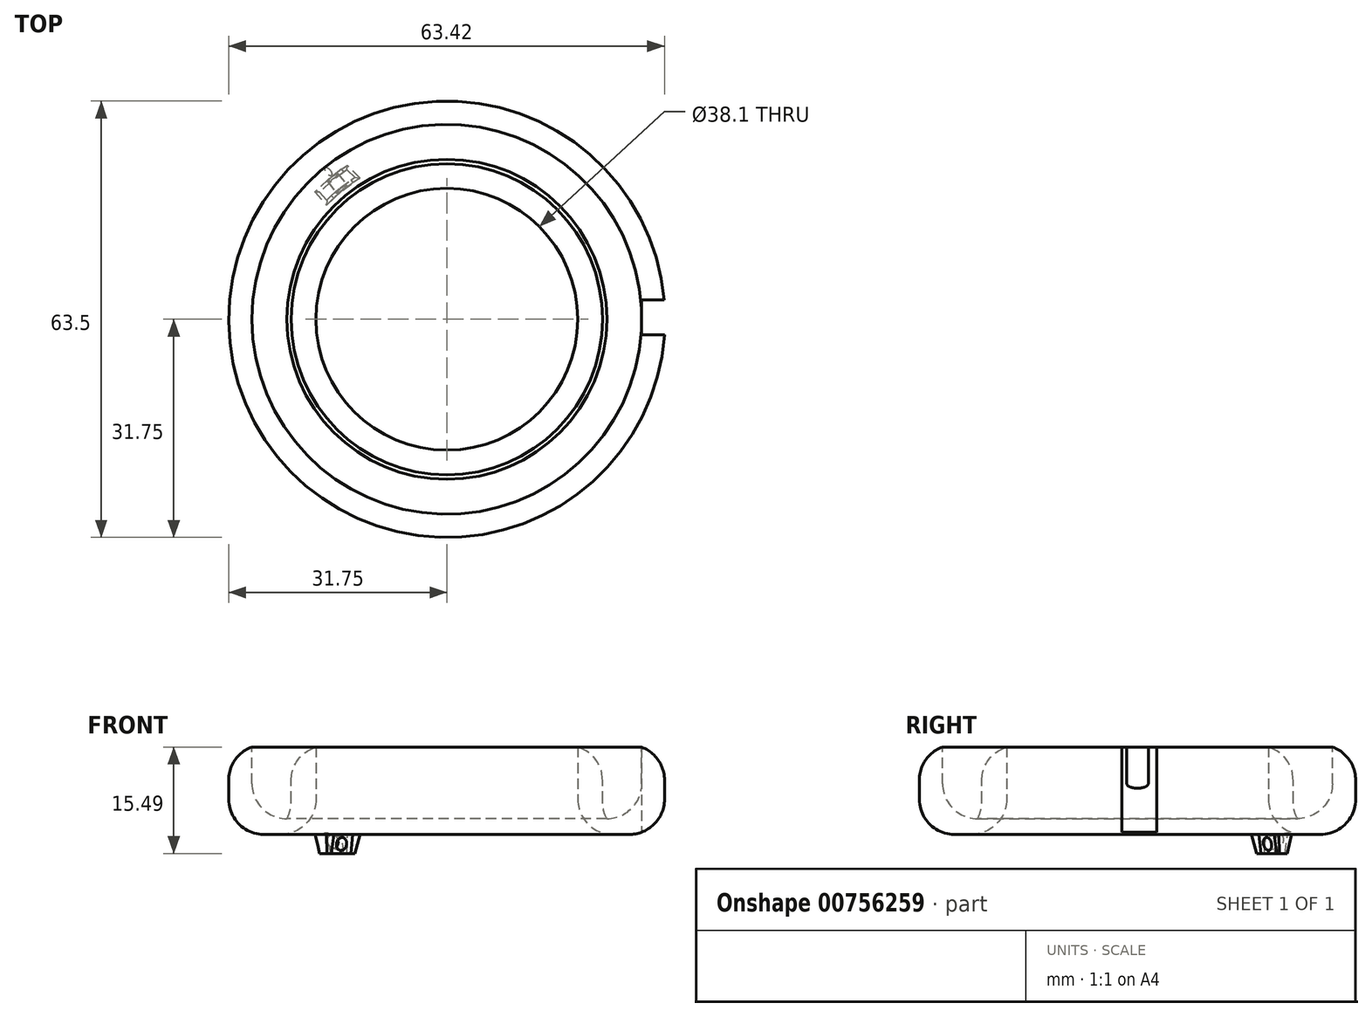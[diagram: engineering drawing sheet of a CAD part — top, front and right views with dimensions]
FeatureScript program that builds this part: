
annotation { "Feature Type Name" : "Feature", "Feature Type Description" : "" }
export const myFeature = defineFeature(function(context is Context, id is Id, definition is map)
    precondition{}
    {
        {
            var Q0;
            Q0=qCreatedBy(makeId("Top.planeOp"),FACE);
            var sketch = newSketch(context, id + "F0", { "sketchPlane" : qUnion([Q0])});
            skCircle(sketch, "E0", {"center": v(0, 0) * mm, "radius": 31.75 * mm});
            skCircle(sketch, "E1", {"center": v(0, 0) * mm, "radius": 19.05 * mm});
            skSolve(sketch);
        }
        {
            var Q0;
            Q0 = qSketchRegion(id + "F0", true);
            extrude(context, id + "F1", {"entities" : qUnion([Q0]), "depth" : 12.7 * mm, "offsetDistance" : 25.4 * mm});
        }
        {
            var Q0;
            Q0=makeQuery(id+"F1.opExtrude","CAP_FACE",FACE,{"disambiguationData":[OSD([sQuery(id+"F0.wireOp",EDGE,"E0"),sQuery(id+"F0.wireOp",EDGE,"E1")])],"isStart":false});
            var sketch = newSketch(context, id + "F2", { "sketchPlane" : qUnion([Q0])});
            skCircle(sketch, "E2", {"center": v(0, 0) * mm, "radius": 22.65 * mm});
            skCircle(sketch, "E3", {"center": v(0, 0) * mm, "radius": 28.37 * mm});
            skSolve(sketch);
        }
        {
            var Q0;
            Q0=makeQuery(id+"F2.imprint","IMPRINT",FACE,{"disambiguationData":[TD([[makeQuery(id+"F2.imprint","IMPRINT",EDGE,{"derivedFrom":sQuery(id+"F2.wireOp",EDGE,"E2")}),-1.0]])]});
            extrude(context, id + "F3", {"entities" : qUnion([Q0]), "operationType" : NewBodyOperationType.REMOVE, "oppositeDirection" : true, "depth" : 10.4 * mm, "offsetDistance" : 25.4 * mm});
        }
        {
            var Q0;
            Q0=makeQuery(id+"F1.opExtrude","CAP_EDGE",EDGE,{"disambiguationData":[OSD([sQuery(id+"F0.wireOp",EDGE,"E0")])],"isStart":true});
            var Q1;
            Q1=makeQuery(id+"F1.opExtrude","CAP_EDGE",EDGE,{"disambiguationData":[OSD([sQuery(id+"F0.wireOp",EDGE,"E0")])],"isStart":false});
            var Q2;
            Q2=makeQuery(id+"F3.boolean.opBoolean","COPY",EDGE,{"derivedFrom":makeQuery(id+"F3.opExtrude","CAP_EDGE",EDGE,{"disambiguationData":[OSD([sQuery(id+"F2.wireOp",EDGE,"E2")])],"isStart":true})});
            fillet(context, id + "F4", {"entities" : qUnion([Q0, Q1, Q2]), "radius" : 5.08 * mm, "tangentPropagation" : true, "allowEdgeOverflow" : false});
        }
        {
            var Q0;
            Q0=qCreatedBy(makeId("Top.planeOp"),FACE);
            var sketch = newSketch(context, id + "F5", { "sketchPlane" : qUnion([Q0])});
            skLineSegment(sketch, "E4", {"start": v(31.94, 2.8) * mm, "end": v(31.94, -2.27) * mm});
            skLineSegment(sketch, "E5", {"start": v(31.94, -2.27) * mm, "end": v(28.32, -2.27) * mm});
            skLineSegment(sketch, "E6", {"start": v(28.32, -2.27) * mm, "end": v(28.32, 0) * mm});
            skLineSegment(sketch, "E7", {"start": v(28.32, 0) * mm, "end": v(28.32, 2.35) * mm});
            skLineSegment(sketch, "E8", {"start": v(28.32, 2.35) * mm, "end": v(28.32, 2.8) * mm});
            skLineSegment(sketch, "E9", {"start": v(28.32, 2.8) * mm, "end": v(31.94, 2.8) * mm});
            skSolve(sketch);
        }
        {
            var Q0;
            Q0 = qSketchRegion(id + "F5", true);
            extrude(context, id + "F6", {"entities" : qUnion([Q0]), "operationType" : NewBodyOperationType.REMOVE, "depth" : 24.6 * mm, "offsetDistance" : 25.4 * mm});
        }
        {
            var Q0;
            Q0=makeQuery(id+"F1.opExtrude","CAP_EDGE",EDGE,{"disambiguationData":[OSD([sQuery(id+"F0.wireOp",EDGE,"E1")])],"isStart":true});
            fillet(context, id + "F7", {"entities" : qUnion([Q0]), "radius" : 5.08 * mm, "tangentPropagation" : true, "allowEdgeOverflow" : false});
        }
        {
            var Q0;
            Q0=makeQuery(id+"F3.boolean.opBoolean","COPY",EDGE,{"derivedFrom":makeQuery(id+"F3.opExtrude","CAP_EDGE",EDGE,{"disambiguationData":[OSD([sQuery(id+"F2.wireOp",EDGE,"E3")])],"isStart":false})});
            fillet(context, id + "F8", {"entities" : qUnion([Q0]), "radius" : 5.08 * mm, "tangentPropagation" : true, "allowEdgeOverflow" : false});
        }
        {
            var Q0;
            Q0=makeQuery(id+"F3.boolean.opBoolean","COPY",EDGE,{"derivedFrom":makeQuery(id+"F3.opExtrude","CAP_EDGE",EDGE,{"disambiguationData":[OSD([sQuery(id+"F2.wireOp",EDGE,"E2")])],"isStart":false})});
            fillet(context, id + "F9", {"entities" : qUnion([Q0]), "radius" : 5.08 * mm, "tangentPropagation" : true, "allowEdgeOverflow" : false});
        }
        {
            var Q0;
            Q0=makeQuery(id+"F1.opExtrude","CAP_FACE",FACE,{"disambiguationData":[OSD([sQuery(id+"F0.wireOp",EDGE,"E0"),sQuery(id+"F0.wireOp",EDGE,"E1")])],"isStart":true});
            var sketch = newSketch(context, id + "F10", { "sketchPlane" : qUnion([Q0])});
            skLineSegment(sketch, "E10", {"start": v(-14.47, -22.4) * mm, "end": v(-12.64, -20.55) * mm});
            skLineSegment(sketch, "E11", {"start": v(-12.64, -20.55) * mm, "end": v(-13.68, -19.87) * mm});
            skLineSegment(sketch, "E12", {"start": v(-13.68, -19.87) * mm, "end": v(-15.2, -18.75) * mm});
            skLineSegment(sketch, "E13", {"start": v(-15.2, -18.75) * mm, "end": v(-16.46, -17.64) * mm});
            skLineSegment(sketch, "E14", {"start": v(-16.46, -17.64) * mm, "end": v(-17.5, -16.61) * mm});
            skLineSegment(sketch, "E15", {"start": v(-17.5, -16.61) * mm, "end": v(-19.19, -18.52) * mm});
            skLineSegment(sketch, "E16", {"start": v(-19.19, -18.52) * mm, "end": v(-18.97, -18.75) * mm});
            skLineSegment(sketch, "E17", {"start": v(-18.97, -18.75) * mm, "end": v(-17.24, -20.35) * mm});
            skLineSegment(sketch, "E18", {"start": v(-17.24, -20.35) * mm, "end": v(-15.3, -21.85) * mm});
            skLineSegment(sketch, "E19", {"start": v(-15.3, -21.85) * mm, "end": v(-14.47, -22.4) * mm});
            skSolve(sketch);
        }
        {
            var Q0;
            Q0 = qSketchRegion(id + "F10", true);
            extrude(context, id + "F11", {"entities" : qUnion([Q0]), "operationType" : NewBodyOperationType.ADD, "depth" : 2.8 * mm, "offsetDistance" : 25.4 * mm, "hasDraft" : true, "draftAngle" : 10 * degree, "draftPullDirection" : true});
        }
        {
            var Q0;
            Q0=makeQuery(id+"F11.opExtrude","SWEPT_FACE",FACE,{"disambiguationData":[OSD([sQuery(id+"F10.wireOp",EDGE,"E12")])]});
            var sketch = newSketch(context, id + "F12", { "sketchPlane" : qUnion([Q0])});
            skCircle(sketch, "E20", {"center": v(-1.66, -5.44) * mm, "radius": 0.96 * mm});
            skSolve(sketch);
        }
        {
            var Q0;
            {var subQ0=sQuery(id+"F12.wireOp",EDGE,"E20");var subQ1=makeQuery(id+"F11.opExtrude","SWEPT_EDGE",EDGE,{"disambiguationData":[OSD([sQuery(id+"F0.wireOp",EDGE,"E0"),sQuery(id+"F0.wireOp",EDGE,"E1"),sQuery(id+"F10.wireOp",EDGE,"E12"),sQuery(id+"F10.wireOp",EDGE,"E13")])]});var subQ2=makeQuery(id+"F12.imprint","INTERSECT",VERTEX,{"disambiguationData":[OD(0.0)],"derivedFrom":[subQ1,subQ0]});Q0=makeQuery(id+"F12.imprint","IMPRINT",FACE,{"disambiguationData":[TD([[makeQuery(id+"F12.imprint","IMPRINT",EDGE,{"disambiguationData":[TD([[subQ2,1.0]])],"derivedFrom":subQ0}),1.0]])]});}
            var Q1;
            {var subQ0=sQuery(id+"F12.wireOp",EDGE,"E20");var subQ1=makeQuery(id+"F11.opExtrude","SWEPT_EDGE",EDGE,{"disambiguationData":[OSD([sQuery(id+"F0.wireOp",EDGE,"E0"),sQuery(id+"F0.wireOp",EDGE,"E1"),sQuery(id+"F10.wireOp",EDGE,"E12"),sQuery(id+"F10.wireOp",EDGE,"E13")])]});var subQ2=makeQuery(id+"F12.imprint","INTERSECT",VERTEX,{"disambiguationData":[OD(0.0)],"derivedFrom":[subQ1,subQ0]});Q1=makeQuery(id+"F12.imprint","IMPRINT",FACE,{"disambiguationData":[TD([[makeQuery(id+"F12.imprint","IMPRINT",EDGE,{"disambiguationData":[TD([[subQ2,-1.0]])],"derivedFrom":subQ0}),1.0]])]});}
            extrude(context, id + "F13", {"entities" : qUnion([Q0, Q1]), "operationType" : NewBodyOperationType.REMOVE, "oppositeDirection" : true, "depth" : 25.4 * mm, "offsetDistance" : 25.4 * mm});
        }
        {
            var Q0;
            Q0=makeQuery(id+"F13.boolean.opBoolean","COPY",FACE,{"derivedFrom":makeQuery(id+"F13.opExtrude","CAP_FACE",FACE,{"disambiguationData":[OSD([sQuery(id+"F12.wireOp",EDGE,"E20")])],"isStart":true})});
            extrude(context, id + "F14", {"entities" : qUnion([Q0]), "operationType" : NewBodyOperationType.REMOVE, "oppositeDirection" : true, "depth" : 25.4 * mm, "offsetDistance" : 25.4 * mm});
        }
    });
